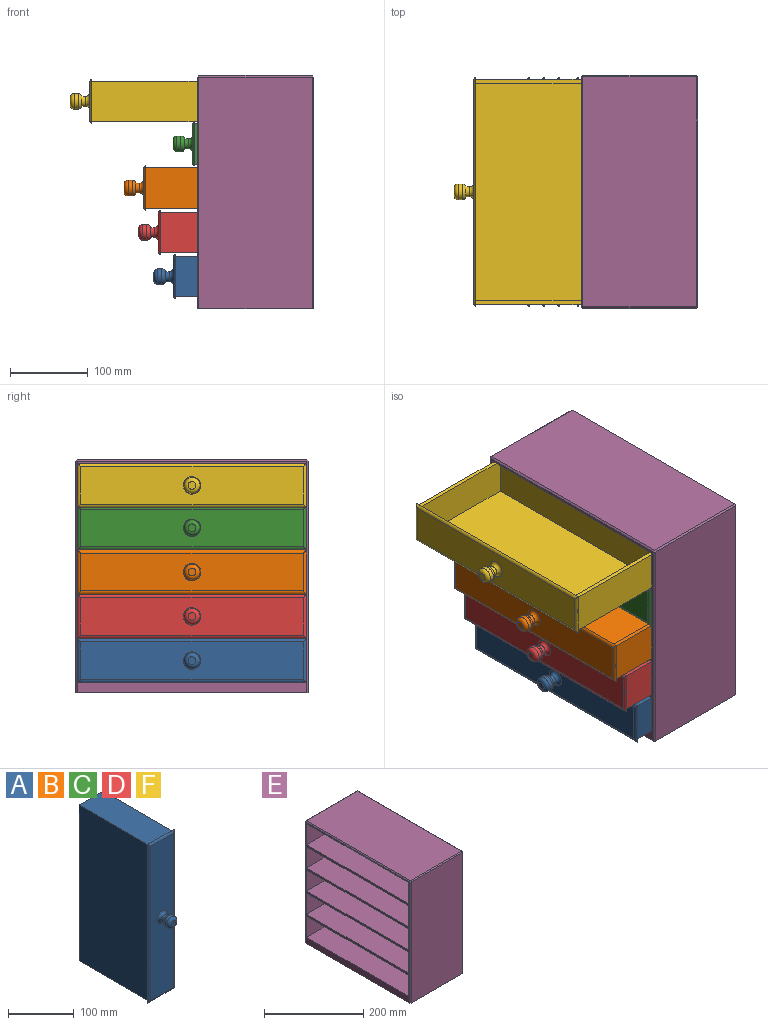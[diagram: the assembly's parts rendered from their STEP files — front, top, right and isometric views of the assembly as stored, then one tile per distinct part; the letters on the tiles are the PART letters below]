
ASSEMBLY  parts=6 mates=5
PART A: 21 faces, bbox 57x177.5x295 mm
  f0: plane 290x150mm, normal (1,0,0), area 2900mm2, adj f1,f3,f4,f6,f7,f8,f9
  f1: plane 150x52mm, normal (0,0,1), area 7800mm2, adj f0,f2,f4,f6
  f2: plane 290x150mm, normal (-1,0,0), area 43500mm2, adj f1,f3,f4,f6
  f3: plane 150x52mm, normal (0,0,-1), area 7800mm2, adj f0,f2,f4,f6
  f4: plane 290x52mm, normal (0,1,0), area 15080mm2, adj f0,f1,f2,f3
  f5: plane 286.34x48.34mm, normal (0,-1,0), area 13444mm2, adj f16,f17,f18,f19,f20
  f6: plane 295x57mm, normal (0,1,0), area 14895mm2, adj f0,f1,f2,f3,f7,f8,f10,f17
  f7: plane 145x47mm, normal (0,0,-1), area 6815mm2, adj f0,f6,f9,f10
  f8: plane 145x47mm, normal (0,0,1), area 6815mm2, adj f0,f6,f9,f10
  f9: plane 280x47mm, normal (0,-1,0), area 13160mm2, adj f0,f7,f8,f10
  f10: plane 280x145mm, normal (1,0,0), area 40600mm2, adj f6,f7,f8,f9
  f11: cylinder r=6.25mm len=12.5mm, axis (0,1,0), area 196.3mm2, adj f14,f16
  f12: plane 10x10mm, normal (0,-1,0), area 78.5mm2, adj f15
  f13: cylinder r=10mm len=20mm, axis (0,1,0), area 324.1mm2, adj f14,f15
  f14: torus R=5mm, axis (0,1,0), area 359.1mm2, adj f11,f13
  f15: torus R=5mm, axis (0,-1,0), area 403.8mm2, adj f12,f13
  f16: torus R=11.25mm, axis (0,-1,0), area 398.1mm2, adj f5,f11
  f17: cylinder r=5mm len=57mm, axis (1,0,0), area 278.1mm2, adj f5,f6,f18,f19
  f18: cylinder r=5mm len=295mm, axis (0,0,-1), area 1524.3mm2, adj f5,f6,f17,f20
  f19: cylinder r=5mm len=295mm, axis (0,0,-1), area 1524.3mm2, adj f5,f6,f17,f20
  f20: cylinder r=5mm len=57mm, axis (1,0,0), area 278.1mm2, adj f5,f6,f18,f19
PART B: same geometry as A
PART C: same geometry as A
PART D: same geometry as A
PART E: 48 faces, bbox 150x300x300 mm
  f0: plane 290x52mm, normal (-1,0,0), area 15080mm2, adj f1,f2,f33,f34
  f1: plane 145x52mm, normal (0,-1,0), area 7540mm2, adj f0,f17,f33,f34
  f2: plane 145x52mm, normal (0,1,0), area 7540mm2, adj f0,f17,f33,f34
  f3: plane 290x52mm, normal (-1,0,0), area 15080mm2, adj f4,f5,f31,f32
  f4: plane 145x52mm, normal (0,-1,0), area 7540mm2, adj f3,f17,f31,f32
  f5: plane 145x52mm, normal (0,1,0), area 7540mm2, adj f3,f17,f31,f32
  f6: plane 290x52mm, normal (-1,0,0), area 15080mm2, adj f7,f8,f29,f30
  f7: plane 145x52mm, normal (0,-1,0), area 7540mm2, adj f6,f17,f29,f30
  f8: plane 145x52mm, normal (0,1,0), area 7540mm2, adj f6,f17,f29,f30
  f9: plane 290x52mm, normal (-1,0,0), area 15080mm2, adj f10,f11,f12,f28
  f10: plane 145x52mm, normal (0,-1,0), area 7540mm2, adj f9,f12,f17,f28
  f11: plane 145x52mm, normal (0,1,0), area 7540mm2, adj f9,f12,f17,f28
  f12: plane 290x145mm, normal (0,0,-1), area 42050mm2, adj f9,f10,f11,f17
  f13: plane 290x52mm, normal (-1,0,0), area 15080mm2, adj f14,f15,f16,f35
  f14: plane 145x52mm, normal (0,1,0), area 7540mm2, adj f13,f16,f17,f35
  f15: plane 145x52mm, normal (0,-1,0), area 7540mm2, adj f13,f16,f17,f35
  f16: plane 290x145mm, normal (0,0,1), area 42050mm2, adj f13,f14,f15,f17
  f17: plane 298x296mm, normal (-1,0,0), area 12808mm2, adj f1,f2,f4,f5,f7,f8,f10,f11
  f18: plane 298x146mm, normal (0,1,0), area 43508mm2, adj f22,f36,f38,f39
  f19: plane 298x146mm, normal (0,-1,0), area 43508mm2, adj f22,f41,f45,f47
  f20: plane 298x296mm, normal (1,0,0), area 88208mm2, adj f22,f36,f40,f41
  f21: plane 296x146mm, normal (0,0,1), area 43216mm2, adj f39,f40,f44,f45
  f22: plane 300x150mm, normal (0,0,-1), area 4392mm2, adj f17,f18,f19,f20,f23,f24,f25,f26
  f23: plane 140x10mm, normal (0,-1,0), area 1400mm2, adj f22,f24,f26,f27
  f24: plane 290x10mm, normal (1,0,0), area 2900mm2, adj f22,f23,f25,f27
  f25: plane 140x10mm, normal (0,1,0), area 1400mm2, adj f22,f24,f26,f27
  f26: plane 290x10mm, normal (-1,0,0), area 2900mm2, adj f22,f23,f25,f27
  f27: plane 290x140mm, normal (0,0,-1), area 40600mm2, adj f23,f24,f25,f26
  f28: plane 290x145mm, normal (0,0,1), area 42050mm2, adj f9,f10,f11,f17
  f29: plane 290x145mm, normal (0,0,-1), area 42050mm2, adj f6,f7,f8,f17
  f30: plane 290x145mm, normal (0,0,1), area 42050mm2, adj f6,f7,f8,f17
  f31: plane 290x145mm, normal (0,0,-1), area 42050mm2, adj f3,f4,f5,f17
  f32: plane 290x145mm, normal (0,0,1), area 42050mm2, adj f3,f4,f5,f17
  f33: plane 290x145mm, normal (0,0,-1), area 42050mm2, adj f0,f1,f2,f17
  f34: plane 290x145mm, normal (0,0,1), area 42050mm2, adj f0,f1,f2,f17
  f35: plane 290x145mm, normal (0,0,-1), area 42050mm2, adj f13,f14,f15,f17
  f36: plane 298x2mm, normal (0.71,0.71,0), area 842.9mm2, adj f18,f20,f22,f37
  f37: plane 2x2mm, normal (0.58,0.58,0.58), area 3.5mm2, adj f36,f39,f40
  f38: plane 298x2mm, normal (-0.71,0.71,0), area 842.9mm2, adj f17,f18,f22,f42
  f39: plane 146x2mm, normal (0,0.71,0.71), area 413mm2, adj f18,f21,f37,f42
  f40: plane 296x2mm, normal (0.71,0,0.71), area 837.2mm2, adj f20,f21,f37,f43
  f41: plane 298x2mm, normal (0.71,-0.71,0), area 842.9mm2, adj f19,f20,f22,f43
  f42: plane 2x2mm, normal (-0.58,0.58,0.58), area 3.5mm2, adj f38,f39,f44
  f43: plane 2x2mm, normal (0.58,-0.58,0.58), area 3.5mm2, adj f40,f41,f45
  f44: plane 296x2mm, normal (-0.71,0,0.71), area 837.2mm2, adj f17,f21,f42,f46
  f45: plane 146x2mm, normal (0,-0.71,0.71), area 413mm2, adj f19,f21,f43,f46
  f46: plane 2x2mm, normal (-0.58,-0.58,0.58), area 3.5mm2, adj f44,f45,f47
  f47: plane 298x2mm, normal (-0.71,-0.71,0), area 842.9mm2, adj f17,f19,f22,f46
PART F: same geometry as A
PLACE A rot(axis=(-0.58,-0.58,-0.58),120deg) t=(46.67,0,41)mm
PLACE B rot(axis=(-0.58,-0.58,-0.58),120deg) t=(8.36,0,155)mm
PLACE C rot(axis=(-0.58,-0.58,-0.58),120deg) t=(71.37,0,212)mm
PLACE D rot(axis=(-0.58,-0.58,-0.58),120deg) t=(27.32,0,98)mm
PLACE E at identity
PLACE F rot(axis=(-0.58,-0.58,-0.58),120deg) t=(-61.07,0,266.64)mm
MATE planar F.f3 <-> E.f11  axis (0,-1,0) through (-136.07,-145,266.64)mm
MATE parallel D.f3 <-> E.f2  axis (0,-1,0) through (-47.68,-145,98)mm
MATE planar C.f3 <-> E.f8  axis (0,-1,0) through (-3.63,-145,212)mm
MATE planar B.f3 <-> E.f5  axis (0,-1,0) through (-66.64,-145,155)mm
MATE parallel A.f1 <-> E.f15  axis (0,1,0) through (-28.33,145,41)mm
